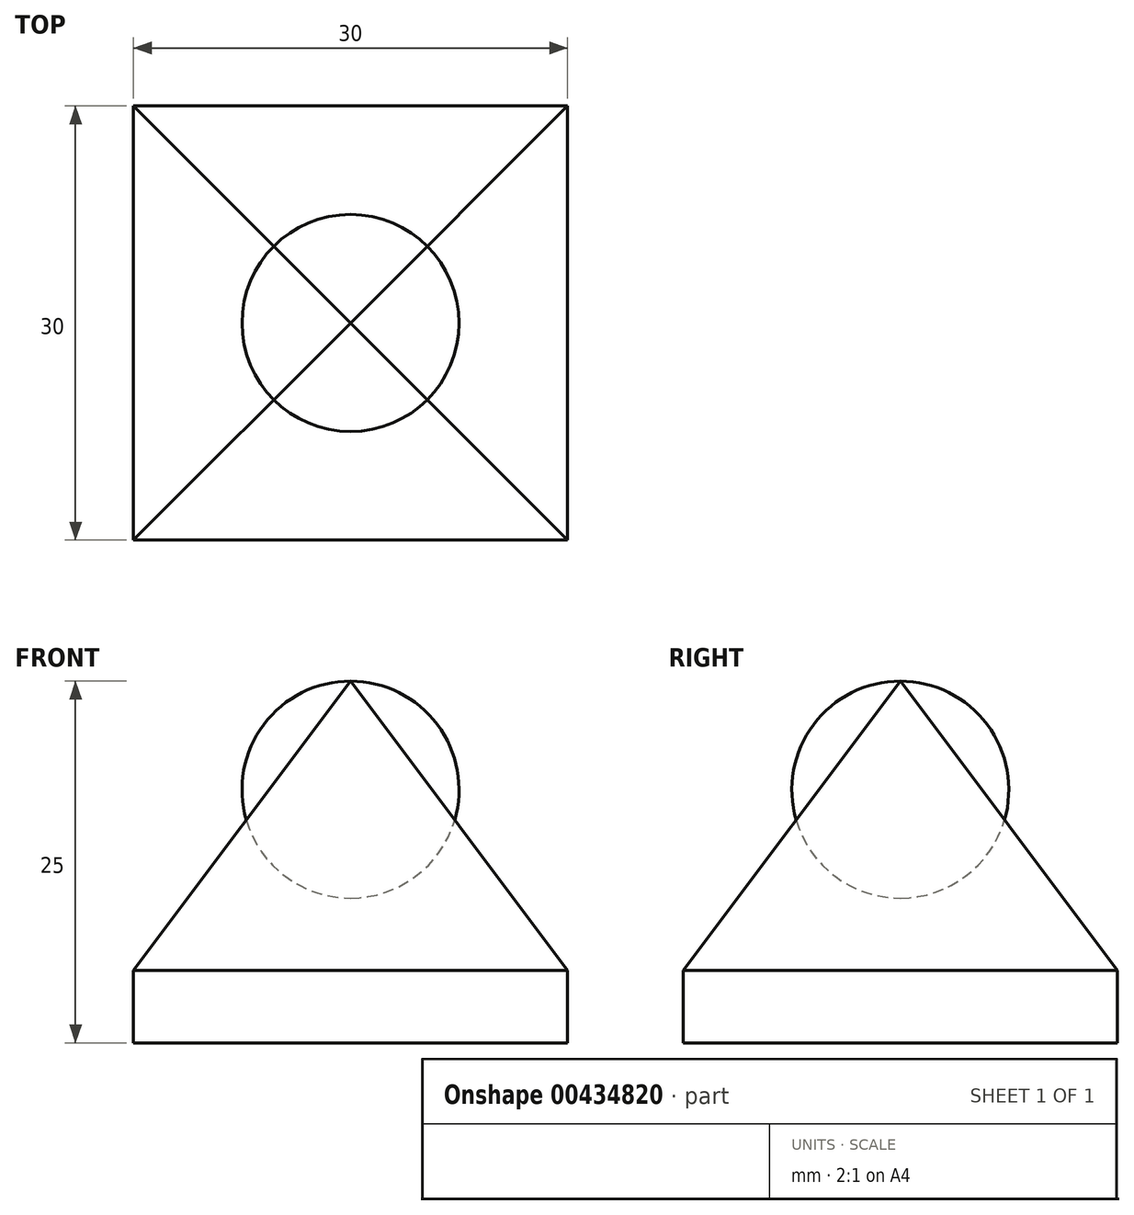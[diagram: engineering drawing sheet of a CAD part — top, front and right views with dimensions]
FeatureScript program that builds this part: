
annotation { "Feature Type Name" : "Feature", "Feature Type Description" : "" }
export const myFeature = defineFeature(function(context is Context, id is Id, definition is map)
    precondition{}
    {
        {
            var Q0;
            Q0=qCreatedBy(makeId("Top.planeOp"),FACE);
            var sketch = newSketch(context, id + "F0", { "sketchPlane" : qUnion([Q0])});
            skLineSegment(sketch, "E0.bottom", {"start": v(-15, 15) * mm, "end": v(15, 15) * mm});
            skLineSegment(sketch, "E0.top", {"start": v(-15, -15) * mm, "end": v(15, -15) * mm});
            skLineSegment(sketch, "E0.left", {"start": v(-15, 15) * mm, "end": v(-15, -15) * mm});
            skLineSegment(sketch, "E0.right", {"start": v(15, 15) * mm, "end": v(15, -15) * mm});
            skLineSegment(sketch, "E1", {"start": v(-15, 15) * mm, "end": v(15, -15) * mm});
            skLineSegment(sketch, "E2", {"start": v(15, 15) * mm, "end": v(-15, -15) * mm});
            skSolve(sketch);
        }
        {
            var Q0;
            {var subQ0=sQuery(id+"F0.wireOp",EDGE,"E0.left");Q0=makeQuery(id+"F0.imprint","IMPRINT",FACE,{"disambiguationData":[TD([[makeQuery(id+"F0.imprint","IMPRINT",EDGE,{"derivedFrom":subQ0}),1.0]])]});}
            var Q1;
            {var subQ0=sQuery(id+"F0.wireOp",EDGE,"E0.bottom");Q1=makeQuery(id+"F0.imprint","IMPRINT",FACE,{"disambiguationData":[TD([[makeQuery(id+"F0.imprint","IMPRINT",EDGE,{"derivedFrom":subQ0}),-1.0]])]});}
            var Q2;
            {var subQ0=sQuery(id+"F0.wireOp",EDGE,"E0.right");Q2=makeQuery(id+"F0.imprint","IMPRINT",FACE,{"disambiguationData":[TD([[makeQuery(id+"F0.imprint","IMPRINT",EDGE,{"derivedFrom":subQ0}),-1.0]])]});}
            var Q3;
            {var subQ0=sQuery(id+"F0.wireOp",EDGE,"E0.top");Q3=makeQuery(id+"F0.imprint","IMPRINT",FACE,{"disambiguationData":[TD([[makeQuery(id+"F0.imprint","IMPRINT",EDGE,{"derivedFrom":subQ0}),1.0]])]});}
            extrude(context, id + "F1", {"entities" : qUnion([Q0, Q1, Q2, Q3]), "depth" : 25 * mm});
        }
        {
            var Q0;
            Q0=makeQuery(id+"F1.opExtrude","SWEPT_FACE",FACE,{"disambiguationData":[OSD([sQuery(id+"F0.wireOp",EDGE,"E0.right")])]});
            var sketch = newSketch(context, id + "F2", { "sketchPlane" : qUnion([Q0])});
            skLineSegment(sketch, "E3.bottom", {"start": v(-15, 0) * mm, "end": v(15, 0) * mm});
            skLineSegment(sketch, "E3.top", {"start": v(-15, 5) * mm, "end": v(15, 5) * mm});
            skLineSegment(sketch, "E3.left", {"start": v(-15, 0) * mm, "end": v(-15, 5) * mm});
            skLineSegment(sketch, "E3.right", {"start": v(15, 0) * mm, "end": v(15, 5) * mm});
            skLineSegment(sketch, "E4", {"start": v(-15, 5) * mm, "end": v(0, 25) * mm});
            skLineSegment(sketch, "E5", {"start": v(0, 25) * mm, "end": v(15, 5) * mm});
            skSolve(sketch);
        }
        {
            var Q0;
            Q0=makeQuery(id+"F1.opExtrude","SWEPT_FACE",FACE,{"disambiguationData":[OSD([sQuery(id+"F0.wireOp",EDGE,"E0.top")])]});
            var sketch = newSketch(context, id + "F3", { "sketchPlane" : qUnion([Q0])});
            skLineSegment(sketch, "E6.bottom", {"start": v(-15, 0) * mm, "end": v(15, 0) * mm});
            skLineSegment(sketch, "E6.top", {"start": v(-15, 5) * mm, "end": v(15, 5) * mm});
            skLineSegment(sketch, "E6.left", {"start": v(-15, 0) * mm, "end": v(-15, 5) * mm});
            skLineSegment(sketch, "E6.right", {"start": v(15, 0) * mm, "end": v(15, 5) * mm});
            skLineSegment(sketch, "E7", {"start": v(-15, 5) * mm, "end": v(0, 25) * mm});
            skLineSegment(sketch, "E8", {"start": v(0, 25) * mm, "end": v(15, 5) * mm});
            skSolve(sketch);
        }
        {
            var Q0;
            {var subQ0=sQuery(id+"F3.wireOp",EDGE,"E7");Q0=makeQuery(id+"F3.imprint","IMPRINT",FACE,{"disambiguationData":[TD([[makeQuery(id+"F3.imprint","IMPRINT",EDGE,{"derivedFrom":subQ0}),1.0]])]});}
            var Q1;
            {var subQ0=sQuery(id+"F3.wireOp",EDGE,"E8");Q1=makeQuery(id+"F3.imprint","IMPRINT",FACE,{"disambiguationData":[TD([[makeQuery(id+"F3.imprint","IMPRINT",EDGE,{"derivedFrom":subQ0}),1.0]])]});}
            extrude(context, id + "F4", {"entities" : qUnion([Q0, Q1]), "operationType" : NewBodyOperationType.REMOVE, "endBound" : BoundingType.THROUGH_ALL, "oppositeDirection" : true, "depth" : 25 * mm});
        }
        {
            var Q0;
            {var subQ0=sQuery(id+"F2.wireOp",EDGE,"E4");Q0=makeQuery(id+"F2.imprint","IMPRINT",FACE,{"disambiguationData":[TD([[makeQuery(id+"F2.imprint","IMPRINT",EDGE,{"derivedFrom":subQ0}),1.0]])]});}
            var Q1;
            {var subQ0=sQuery(id+"F2.wireOp",EDGE,"E5");Q1=makeQuery(id+"F2.imprint","IMPRINT",FACE,{"disambiguationData":[TD([[makeQuery(id+"F2.imprint","IMPRINT",EDGE,{"derivedFrom":subQ0}),1.0]])]});}
            extrude(context, id + "F5", {"entities" : qUnion([Q0, Q1]), "operationType" : NewBodyOperationType.REMOVE, "endBound" : BoundingType.THROUGH_ALL, "oppositeDirection" : true, "depth" : 25 * mm});
        }
        {
            var Q0;
            Q0=qCreatedBy(makeId("Front.planeOp"),FACE);
            var sketch = newSketch(context, id + "F6", { "sketchPlane" : qUnion([Q0])});
            skCircle(sketch, "E9", {"center": v(0, 17.5) * mm, "radius": 7.5 * mm});
            skPoint(sketch, "E9.first.point", {"position": v(-7.15, 19.76) * mm});
            skPoint(sketch, "E9.second.point", {"position": v(7.34, 19.02) * mm});
            skPoint(sketch, "E9.third.point", {"position": v(0, 10) * mm});
            skLineSegment(sketch, "E10", {"start": v(0, 10) * mm, "end": v(0, 25) * mm});
            skSolve(sketch);
        }
        {
            var Q0;
            {var subQ0=sQuery(id+"F6.wireOp",EDGE,"E10");Q0=makeQuery(id+"F6.imprint","IMPRINT",FACE,{"disambiguationData":[TD([[makeQuery(id+"F6.imprint","IMPRINT",EDGE,{"derivedFrom":subQ0}),-1.0]])]});}
            var Q1;
            Q1=sQuery(id+"F6.wireOp",EDGE,"E10");
            revolve(context, id + "F7", {"entities" : qUnion([Q0]), "axis" : qUnion([Q1]), "revolveType" : RevolveType.FULL});
        }
    });
